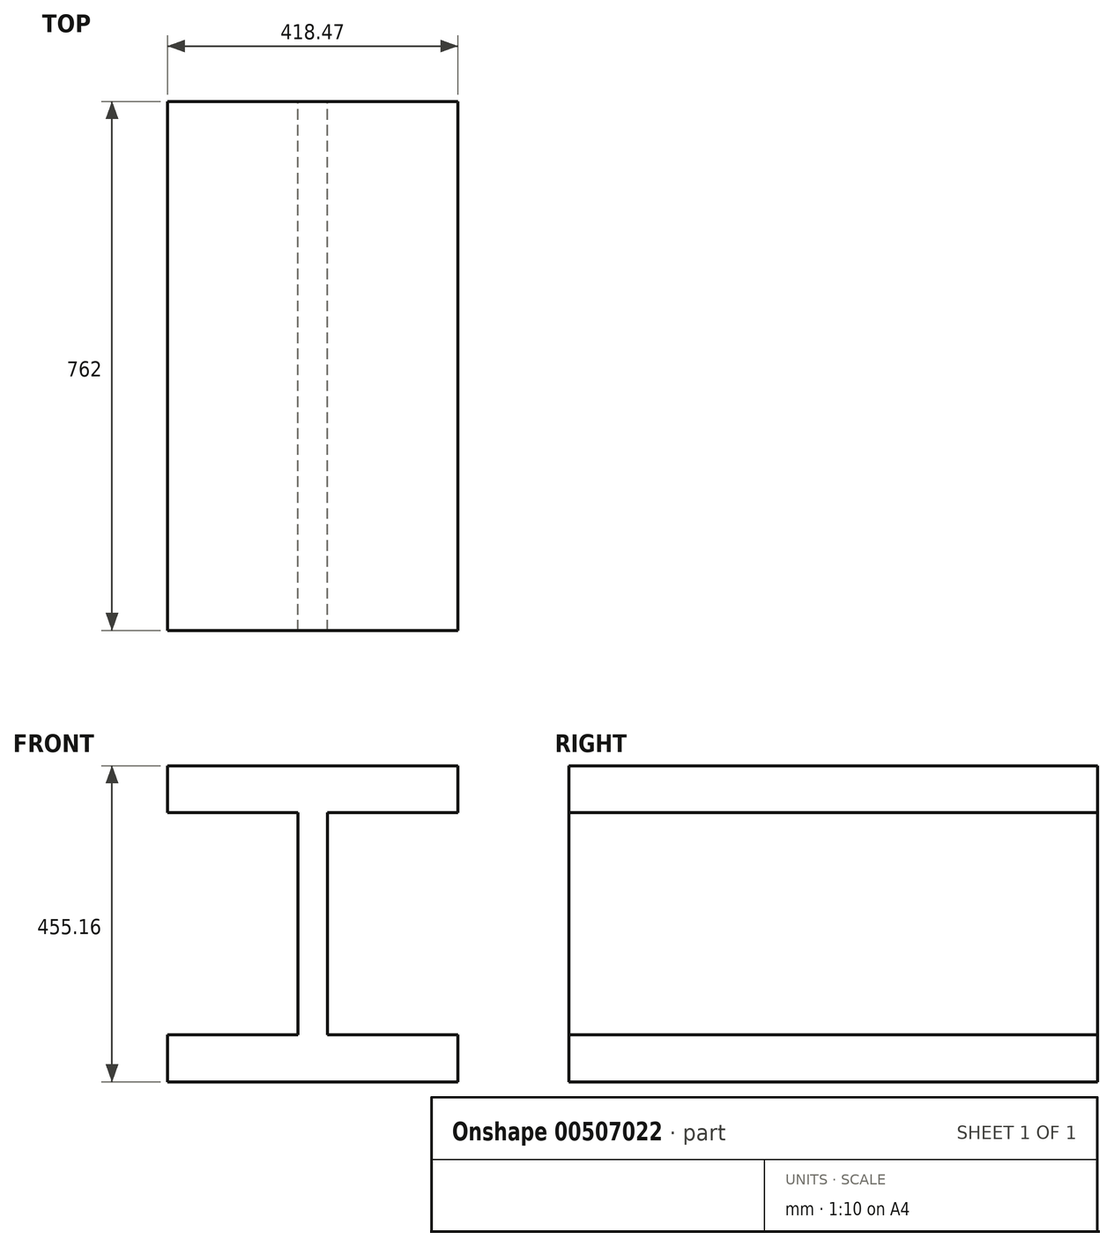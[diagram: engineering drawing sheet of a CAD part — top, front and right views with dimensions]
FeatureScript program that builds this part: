
annotation { "Feature Type Name" : "Feature", "Feature Type Description" : "" }
export const myFeature = defineFeature(function(context is Context, id is Id, definition is map)
    precondition{}
    {
        {
            var Q0;
            Q0=qCreatedBy(makeId("Front.planeOp"),FACE);
            var sketch = newSketch(context, id + "F0", { "sketchPlane" : qUnion([Q0])});
            skLineSegment(sketch, "E0", {"start": v(97.3, 84.08) * mm, "end": v(-111.93, 84.08) * mm});
            skLineSegment(sketch, "E1", {"start": v(-111.93, 84.08) * mm, "end": v(-111.93, 16.52) * mm});
            skLineSegment(sketch, "E2", {"start": v(-111.93, 16.52) * mm, "end": v(76.29, 16.52) * mm});
            skLineSegment(sketch, "E3", {"start": v(76.29, 16.52) * mm, "end": v(76.29, -143.5) * mm});
            skLineSegment(sketch, "E4", {"start": v(97.3, 206.8) * mm, "end": v(97.3, -143.5) * mm, "construction": true});
            skLineSegment(sketch, "E5", {"start": v(97.3, -143.5) * mm, "end": v(-153.43, -143.5) * mm, "construction": true});
            skLineSegment(sketch, "E6.MirrorCS", {"start": v(97.3, -143.5) * mm, "end": v(348.04, -143.5) * mm, "construction": true});
            skLineSegment(sketch, "E7.MirrorCS", {"start": v(97.3, 84.08) * mm, "end": v(306.54, 84.08) * mm});
            skLineSegment(sketch, "E8.MirrorCS", {"start": v(306.54, 84.08) * mm, "end": v(306.54, 16.52) * mm});
            skLineSegment(sketch, "E9.MirrorCS", {"start": v(306.54, 16.52) * mm, "end": v(118.32, 16.52) * mm});
            skLineSegment(sketch, "E10.MirrorCS", {"start": v(118.32, 16.52) * mm, "end": v(118.32, -143.5) * mm});
            skLineSegment(sketch, "E11.MirrorCS", {"start": v(76.29, -303.52) * mm, "end": v(76.29, -143.5) * mm});
            skLineSegment(sketch, "E12.MirrorCS", {"start": v(-111.93, -303.52) * mm, "end": v(76.29, -303.52) * mm});
            skLineSegment(sketch, "E13.MirrorCS", {"start": v(-111.93, -371.08) * mm, "end": v(-111.93, -303.52) * mm});
            skLineSegment(sketch, "E14.MirrorCS", {"start": v(97.3, -371.08) * mm, "end": v(-111.93, -371.08) * mm});
            skLineSegment(sketch, "E15.MirrorCS", {"start": v(118.32, -303.52) * mm, "end": v(118.32, -143.5) * mm});
            skLineSegment(sketch, "E16.MirrorCS", {"start": v(306.54, -303.52) * mm, "end": v(118.32, -303.52) * mm});
            skLineSegment(sketch, "E17.MirrorCS", {"start": v(306.54, -371.08) * mm, "end": v(306.54, -303.52) * mm});
            skLineSegment(sketch, "E18.MirrorCS", {"start": v(97.3, -371.08) * mm, "end": v(306.54, -371.08) * mm});
            skSolve(sketch);
        }
        {
            var Q0;
            Q0 = qSketchRegion(id + "F0", true);
            extrude(context, id + "F1", {"entities" : qUnion([Q0]), "depth" : 762 * mm});
        }
    });
